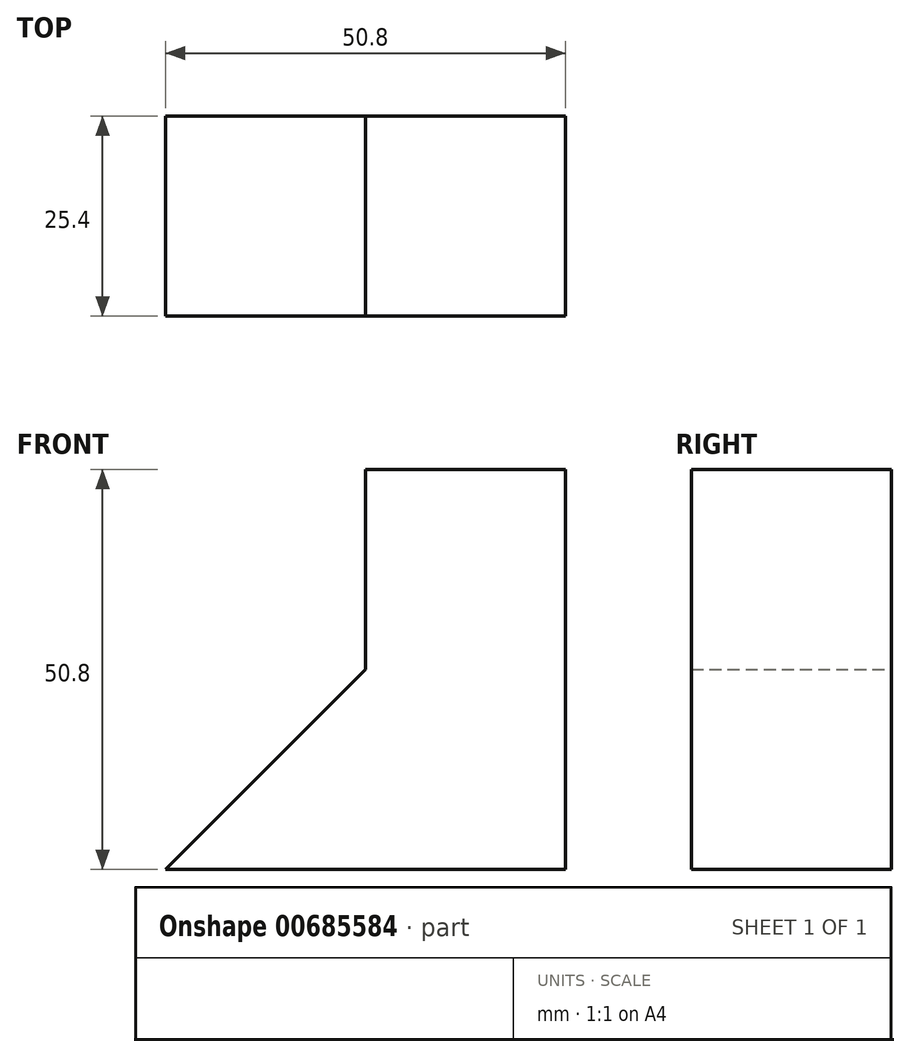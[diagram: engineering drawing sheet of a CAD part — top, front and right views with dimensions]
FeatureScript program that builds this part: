
annotation { "Feature Type Name" : "Feature", "Feature Type Description" : "" }
export const myFeature = defineFeature(function(context is Context, id is Id, definition is map)
    precondition{}
    {
        {
            var Q0;
            Q0=qCreatedBy(makeId("Front.planeOp"),FACE);
            var sketch = newSketch(context, id + "F0", { "sketchPlane" : qUnion([Q0])});
            skLineSegment(sketch, "E0", {"start": v(0, 0) * mm, "end": v(0, 50.8) * mm});
            skLineSegment(sketch, "E1", {"start": v(0, 0) * mm, "end": v(-50.8, 0) * mm});
            skLineSegment(sketch, "E2", {"start": v(0, 50.8) * mm, "end": v(-25.4, 50.8) * mm});
            skLineSegment(sketch, "E3", {"start": v(-25.4, 50.8) * mm, "end": v(-25.4, 25.4) * mm});
            skLineSegment(sketch, "E4", {"start": v(-50.8, 0) * mm, "end": v(-25.4, 25.4) * mm});
            skSolve(sketch);
        }
        {
            var Q0;
            Q0 = qSketchRegion(id + "F0", true);
            extrude(context, id + "F1", {"entities" : qUnion([Q0]), "depth" : 25.4 * mm, "offsetDistance" : 25.4 * mm});
        }
    });
